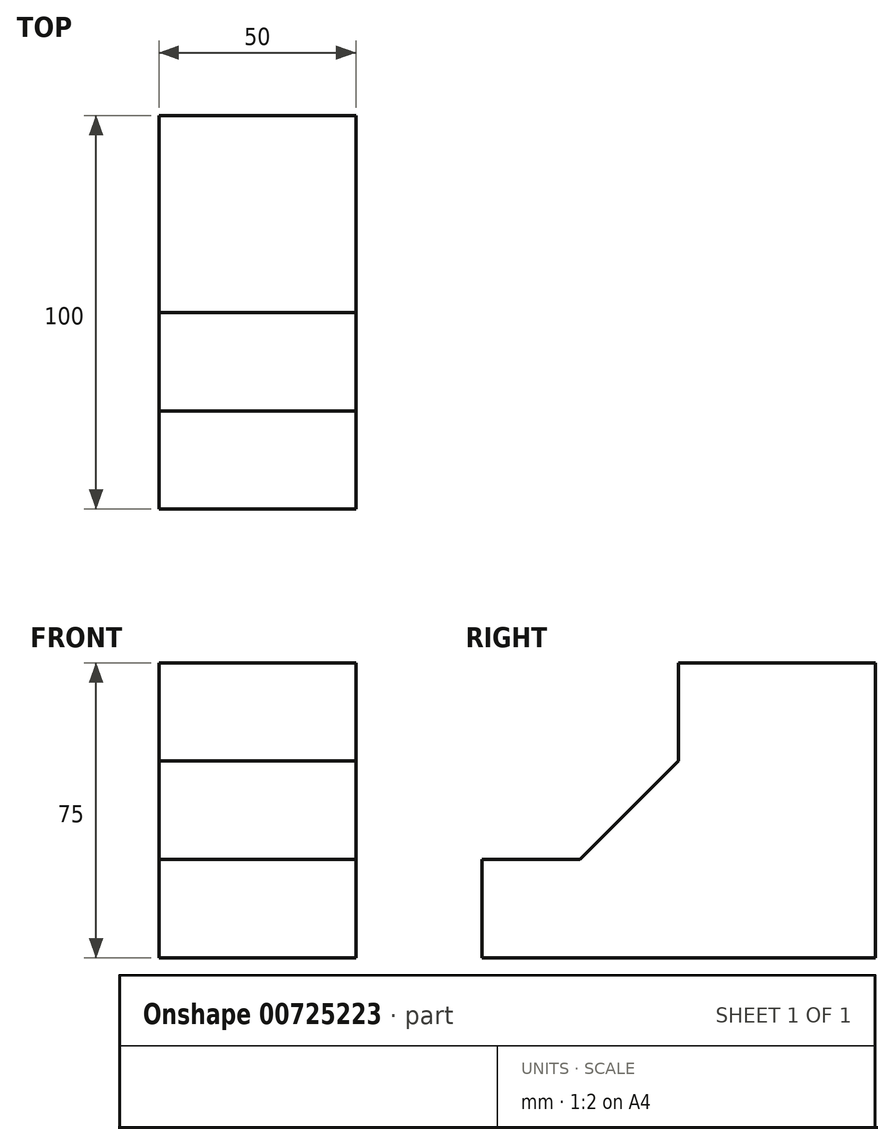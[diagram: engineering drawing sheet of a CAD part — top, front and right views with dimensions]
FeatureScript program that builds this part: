
annotation { "Feature Type Name" : "Feature", "Feature Type Description" : "" }
export const myFeature = defineFeature(function(context is Context, id is Id, definition is map)
    precondition{}
    {
        {
            var Q0;
            Q0=qCreatedBy(makeId("Right.planeOp"),FACE);
            var sketch = newSketch(context, id + "F0", { "sketchPlane" : qUnion([Q0])});
            skLineSegment(sketch, "E0", {"start": v(0, 0) * mm, "end": v(0, 25) * mm});
            skLineSegment(sketch, "E1", {"start": v(25, 25) * mm, "end": v(0, 25) * mm});
            skLineSegment(sketch, "E2", {"start": v(50, 50) * mm, "end": v(25, 25) * mm});
            skLineSegment(sketch, "E3", {"start": v(50, 75) * mm, "end": v(50, 50) * mm});
            skLineSegment(sketch, "E4", {"start": v(50, 75) * mm, "end": v(100, 75) * mm});
            skLineSegment(sketch, "E5", {"start": v(100, 75) * mm, "end": v(100, 75) * mm});
            skLineSegment(sketch, "E6", {"start": v(100, 0) * mm, "end": v(100, 75) * mm});
            skLineSegment(sketch, "E7", {"start": v(0, 0) * mm, "end": v(0.49, 0.5) * mm});
            skLineSegment(sketch, "E8", {"start": v(100, 0) * mm, "end": v(0, 0) * mm});
            skSolve(sketch);
        }
        {
            var Q0;
            Q0=makeQuery(id+"F0.imprint","IMPRINT",FACE,{"disambiguationData":[TD([[makeQuery(id+"F0.imprint","IMPRINT",EDGE,{"derivedFrom":sQuery(id+"F0.wireOp",EDGE,"E0")}),-1.0]])]});
            extrude(context, id + "F1", {"entities" : qUnion([Q0]), "depth" : 50 * mm, "offsetDistance" : 25 * mm});
        }
    });
